# Revit family: Lighting-Track-Reggiani-Yori_60mm-10W
name_source: partatom
category: Apparecchi per illuminazione
revit_build: Autodesk Revit 2015 (Build: 20140323_1530(x64)
units: mm (PartAtom-declared; Revit-internal decimal feet)

## types (2) — shared parameters
Angolo inclinazione = 90.00°
BIMobject category = Lighting
Box internal = Reggiani Nero
Data Sheet = http://www.reggiani.net
Date of publishing = 2015-10-01
Descrizione = Minimalism and rigour in the service of functionality, Yori is a high performance luminaire with a compact footprint. Two simple bodies combined by a simple joint allow the optical section to be adjusted. Yori is designed for the most innovative LED and metal halide lamps, and is configured for mounting on tracks, inside channels, recessed, onto surfaces and inside grooves in ceilings, thanks to the new versi ...
Design country = Italy
Edition number = 1
File diagramma fotometrico = TD921_HW_LED_15 deegrees beam._3000K_803lm_CRI90.ies
Filtro dei colori = 16777215
IFC Classification = Light Fixture
Installation instructions = http://www.reggiani.net
Lampada = Led
Lens = Lente Yori polic trasparente
Lens frame = Reggiani Nero
Manufacturer country = Italy
Manufacturer name = Reggiani
Material main = Aluminium
Material secondary = Glass
Nominal height = 90
Nominal width = 60
Product Guid = a4baa793-f88c-4ca5-a32b-6ffec7d65a65
Product SKU = yori_track_60
Product data url = http://bimobject.com
Product family = Track fixture
Product group = Yori
Produttore = Reggiani illuminazione spa
QR code = http://bimobject.com
Ring = Reggiani Nero
Technical description = http://www.reggiani.net
UNSPSC Code = 3911
URL = http://www.reggiani.net
URL to photometrics = http://bimobject.com
Variazione temperatura colore lampada con luminosità attenuata = <Nessuno>
Weight Net (Kg) = 0.55
control = Ø. = ON/OFF, D. = DALI, V. = DIMM 1-10V, T

## per-type parameters (varying)
| type | Box closed | Docking | Docking up | Modello | UNSPSC name |
| Reggiani Yori TD92 white 10 w | Reggiani Bianco | Reggiani Bianco | Reggiani Bianco | Reggiani Yori  TD 92w | Lighting Fixtures and Accessories |
| Reggiani Yori TD92 Black  10 w | Reggiani Nero | Reggiani Nero | Reggiani Nero | Reggiani Yori  TD 92 w |  |

## geometry (parser evidence)
native form markers: Blend x8
no freeform markers — native parametric forms only
